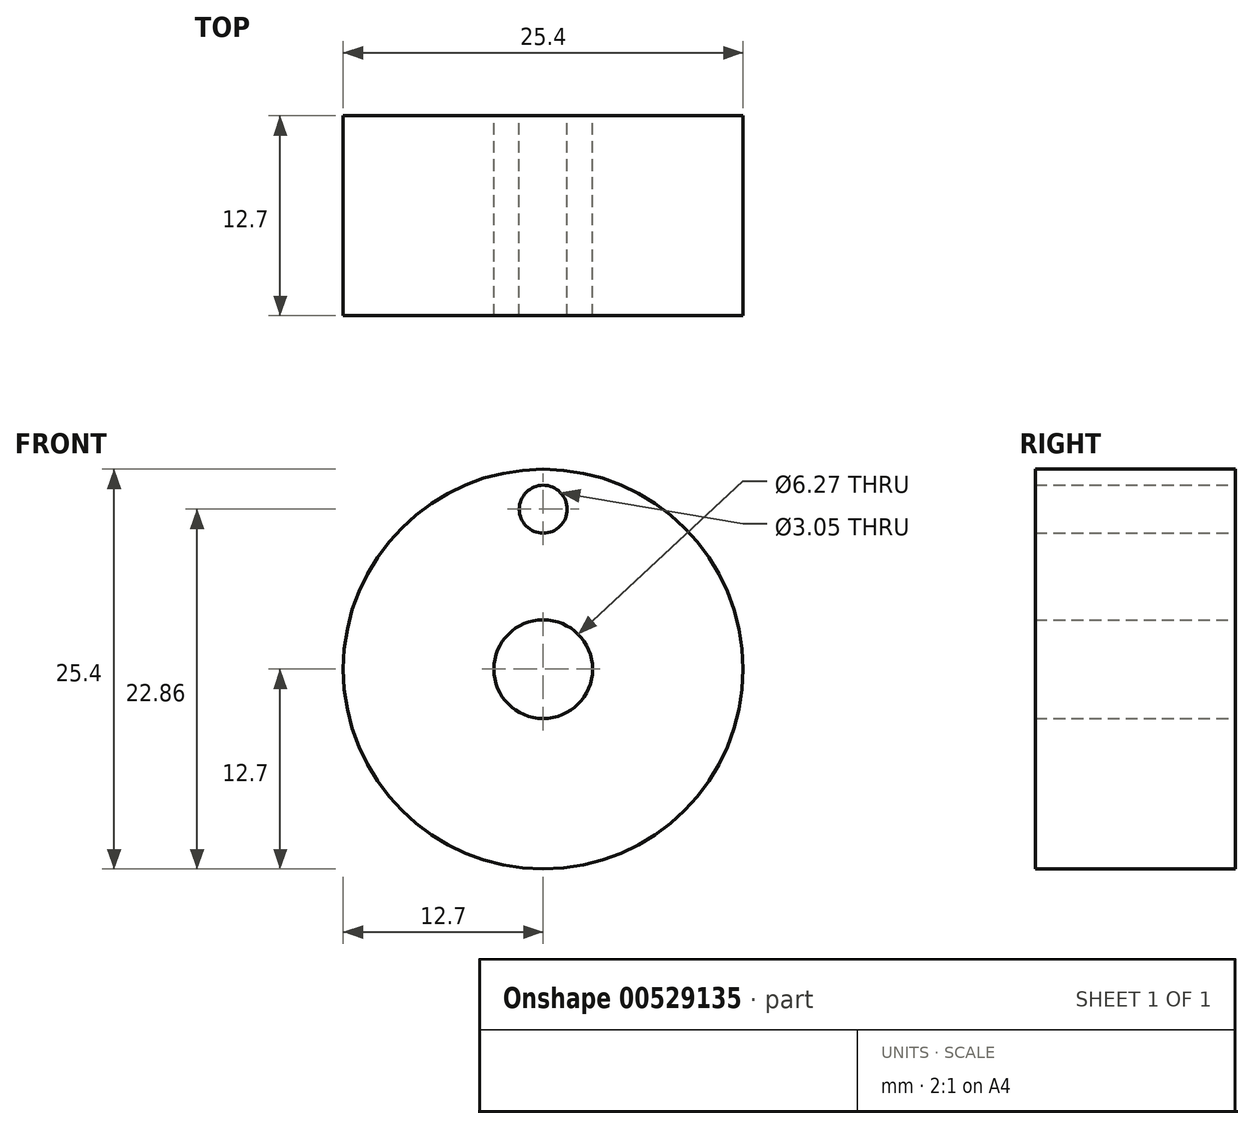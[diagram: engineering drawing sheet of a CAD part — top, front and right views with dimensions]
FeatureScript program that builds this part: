
annotation { "Feature Type Name" : "Feature", "Feature Type Description" : "" }
export const myFeature = defineFeature(function(context is Context, id is Id, definition is map)
    precondition{}
    {
        {
            var Q0;
            Q0=qCreatedBy(makeId("Front.planeOp"),FACE);
            var sketch = newSketch(context, id + "F0", { "sketchPlane" : qUnion([Q0])});
            skCircle(sketch, "E0", {"center": v(0, 0) * mm, "radius": 12.7 * mm});
            skCircle(sketch, "E1", {"center": v(0, 0) * mm, "radius": 3.14 * mm});
            skCircle(sketch, "E2", {"center": v(0, 10.16) * mm, "radius": 1.52 * mm});
            skLineSegment(sketch, "E3", {"start": v(0, 0) * mm, "end": v(0, 12.7) * mm, "construction": true});
            skSolve(sketch);
        }
        {
            var Q0;
            Q0 = qSketchRegion(id + "F0", true);
            extrude(context, id + "F1", {"entities" : qUnion([Q0]), "depth" : 12.7 * mm, "offsetDistance" : 25.4 * mm});
        }
    });
